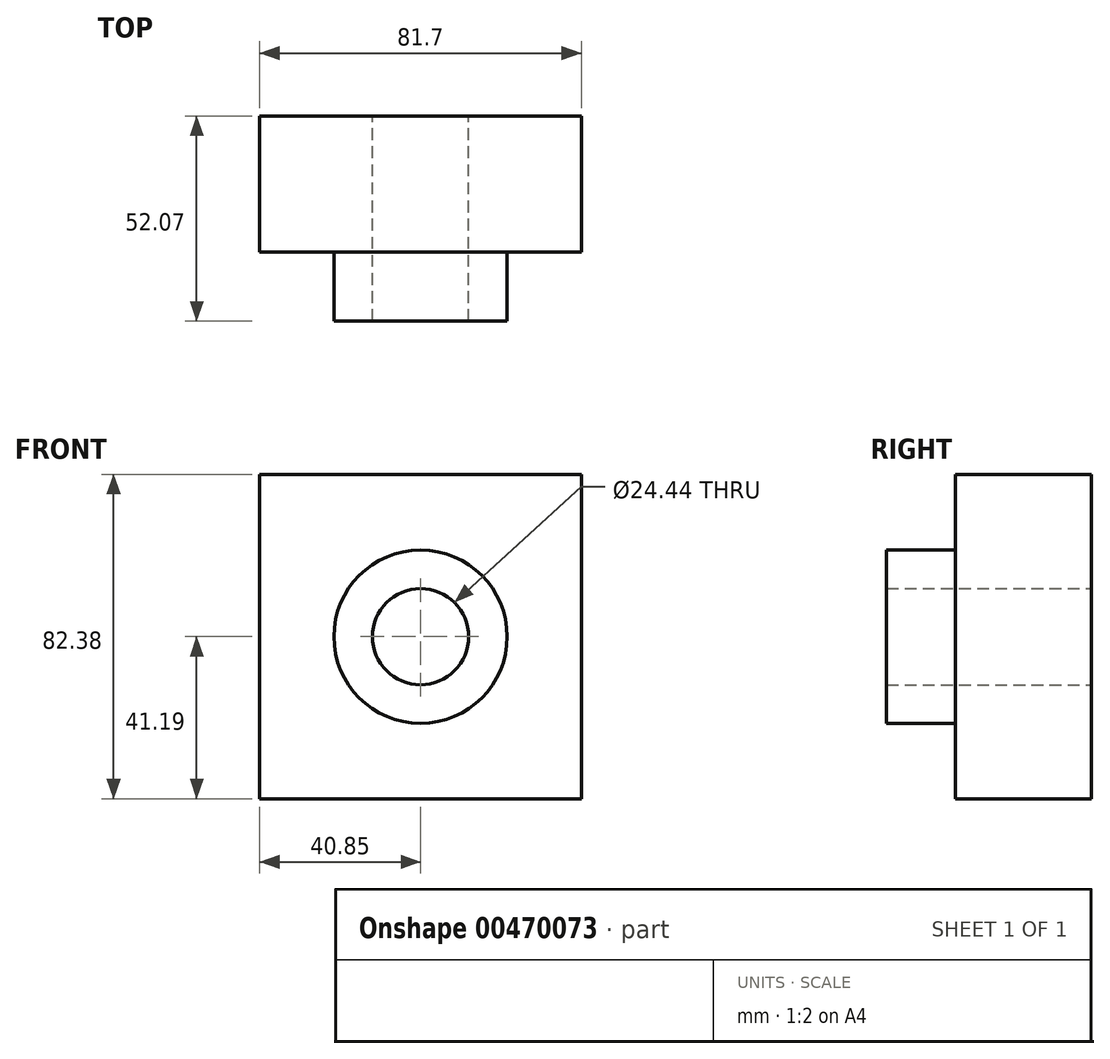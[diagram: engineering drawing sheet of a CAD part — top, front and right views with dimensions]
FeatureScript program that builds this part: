
annotation { "Feature Type Name" : "Feature", "Feature Type Description" : "" }
export const myFeature = defineFeature(function(context is Context, id is Id, definition is map)
    precondition{}
    {
        {
            var Q0;
            Q0=qCreatedBy(makeId("Front.planeOp"),FACE);
            var sketch = newSketch(context, id + "F0", { "sketchPlane" : qUnion([Q0])});
            skLineSegment(sketch, "E0.bottom", {"start": v(-40.85, 41.2) * mm, "end": v(40.85, 41.2) * mm});
            skLineSegment(sketch, "E0.top", {"start": v(-40.85, -41.2) * mm, "end": v(40.85, -41.2) * mm});
            skLineSegment(sketch, "E0.left", {"start": v(-40.85, 41.2) * mm, "end": v(-40.85, -41.2) * mm});
            skLineSegment(sketch, "E0.right", {"start": v(40.85, 41.2) * mm, "end": v(40.85, -41.2) * mm});
            skPoint(sketch, "E0.middle", {"position": v(0, 0) * mm});
            skCircle(sketch, "E1", {"center": v(0, 0) * mm, "radius": 22.02 * mm});
            skCircle(sketch, "E2", {"center": v(0, 0) * mm, "radius": 12.22 * mm});
            skSolve(sketch);
        }
        {
            var Q0;
            Q0=makeQuery(id+"F0.imprint","IMPRINT",FACE,{"disambiguationData":[TD([[makeQuery(id+"F0.imprint","IMPRINT",EDGE,{"derivedFrom":sQuery(id+"F0.wireOp",EDGE,"E0.bottom")}),-1.0]])]});
            extrude(context, id + "F1", {"entities" : qUnion([Q0]), "depth" : 34.54 * mm});
        }
        {
            var Q0;
            Q0=makeQuery(id+"F0.imprint","IMPRINT",FACE,{"disambiguationData":[TD([[makeQuery(id+"F0.imprint","IMPRINT",EDGE,{"derivedFrom":sQuery(id+"F0.wireOp",EDGE,"E1")}),1.0]])]});
            extrude(context, id + "F2", {"entities" : qUnion([Q0]), "operationType" : NewBodyOperationType.ADD, "depth" : 52.07 * mm});
        }
        {
            var Q0;
            Q0=makeQuery(id+"F0.imprint","IMPRINT",FACE,{"disambiguationData":[TD([[makeQuery(id+"F0.imprint","IMPRINT",EDGE,{"derivedFrom":sQuery(id+"F0.wireOp",EDGE,"E2")}),1.0]])]});
            extrude(context, id + "F3", {"entities" : qUnion([Q0]), "operationType" : NewBodyOperationType.REMOVE, "endBound" : BoundingType.THROUGH_ALL, "oppositeDirection" : true, "depth" : 25.4 * mm});
        }
    });
